# Revit family: Maxlogic Extinguishant manual release button
name_source: partatom
category: Fire Alarm Devices
units: mm (PartAtom-declared; Revit-internal decimal feet)

## family parameters
Cut with Voids When Loaded = No
Host = Face
Maintain Annotation Orientation = Yes
OmniClass Number = 23.85.30.21
OmniClass Title = Environmental Detection/Registration
Part Type = Normal
Room Calculation Point = No
Round Connector Dimension = Use Diameter
Shared = No

## types (1)
- Maxlogic Extinguishant manual release button
    Code Performance = EN 12094-3
    Color = Yellow
    Cost = 0 $
    Default Elevation = 0 mm  [stored 0 ft]
    Description = Extinguishant manual release button
    Fax Number = (+)90 216 466 45 10
    Installation Manual = https://mavilielektronik.com
    Main Material = Yellow Plastic ABS
    Manufacturer = Mavili Elektronik Ticaret A.Ş.
    Model = MaxLogic
    Mounting height = 140 cm above from ground (+/-200mm)
    Mounting surface = Wall mounting
    Nominal Depth = 58 mm
    Nominal Height = 91 mm
    Nominal Width = 87 mm
    Operating temperature = (-10°C) - (+55°C)
    Operating voltage range = 10-30 V/DC
    Operatonal Voltage (default) = 24 V/DC
    Product Code = ML-2710.MR
    Protection Sign = IP22D
    Protective Cover = ML-0710
    Public Works Pose Number = 833-260
    Secondary Material = Plastic
    URL = https://www.mavili.com.tr
    Warranty Duration Labor = 2
    Warranty Duration Parts = 2
    Warranty Duration Unit = Year
    Weight = 140 gr.

note: [stored X ft] marks values corroborated as IEEE doubles in the binary element streams (Revit-internal decimal feet)

## geometry (parser evidence)
native form markers: Sweep x3
no freeform markers — native parametric forms only
